# Revit family: NITRO - Mezcladora
name_source: partatom
category: Aparatos sanitarios
revit_build: Autodesk Revit 2016 (Build: 20150220_1215(x64)
units: mm (PartAtom-declared; Revit-internal decimal feet)

## family parameters
Anfitrión = Muro
Compartido = No
Corte con vacíos al cargar = No
Cota de conector redondo = Diámetro de uso
Número OmniClass = 23.45.05.14.14
Punto de cálculo de habitación = No
Siempre vertical = Sí
Tipo de pieza = Normal
Título OmniClass = Sinks/Lavatories

## types (1)
- NITRO Mezcladora
    Accionamiento = Por maneta
    CWFU = 1
    Caudal = 6.0 L/min
    Cierre = Manual
    Comentarios de tipo = Columna no regulable en altura.
    Código de montaje = D2020
    Descripción = Grupo ducha mezcladora con columna, rociador y accesorios ducha.
    Diámetro entrada = 1"
    Fabricante = GALINDO
    HWFU = 1
    Material = Latón, cromado
    Modelo = NITRO Mezcladora
    Notas de suministro = Suministrado con excéntricas 1/2” a 3/4” , flexo, soporte a pared y maneral.
    Referencia = 52450300
    Sistema = AFS / ACS
    Teléfono = +34 93 680 13 15
    URL = http://www.griferiasgalindo.com
    WFU = 0

## geometry (parser evidence)
native form markers: Blend x4
no freeform markers — native parametric forms only
